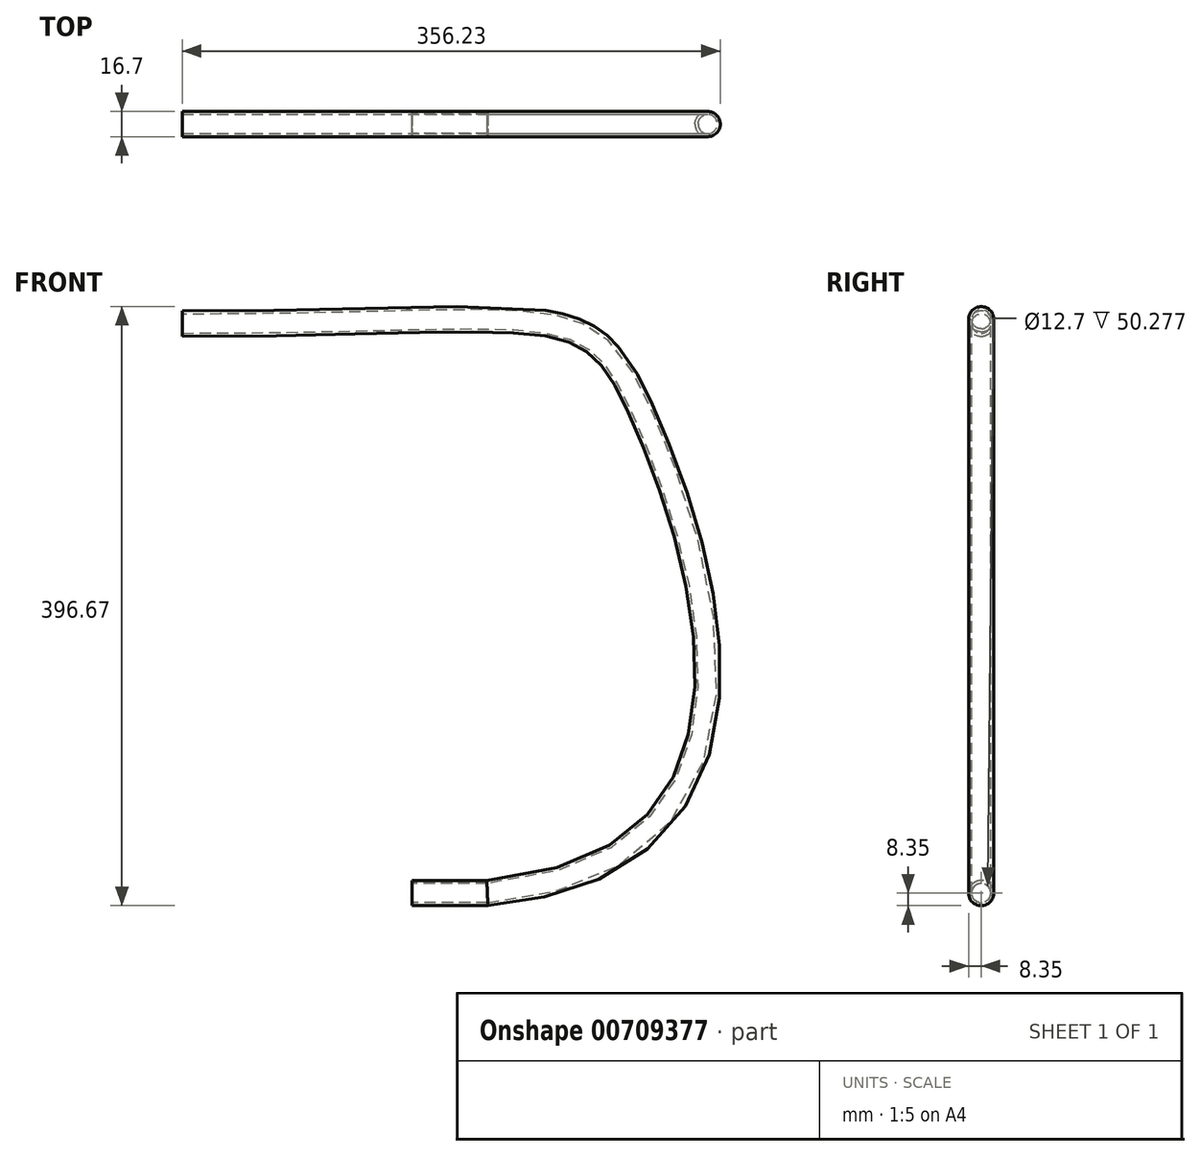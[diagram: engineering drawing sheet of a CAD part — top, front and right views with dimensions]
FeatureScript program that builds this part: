
annotation { "Feature Type Name" : "Feature", "Feature Type Description" : "" }
export const myFeature = defineFeature(function(context is Context, id is Id, definition is map)
    precondition{}
    {
        {
            var Q0;
            Q0=qCreatedBy(makeId("Front.planeOp"),FACE);
            var sketch = newSketch(context, id + "F0", { "sketchPlane" : qUnion([Q0])});
            skPoint(sketch, "E0", {"position": v(-398.72, 63.1) * mm});
            skPoint(sketch, "E1", {"position": v(-246.72, 63.1) * mm});
            skPoint(sketch, "E2", {"position": v(-246.72, -313.9) * mm});
            skLineSegment(sketch, "E3", {"start": v(-246.72, -313.9) * mm, "end": v(-196.72, -313.9) * mm});
            skFitSpline(sketch, "E4", {"points": [v(-398.72, 63.1) * mm, v(-92.27, 0) * mm, v(-196.72, -313.9) * mm], "startDerivative": vector(1557.66, 0) * mm, "endDerivative": vector(-1237.9, -107.97) * mm});
            skSolve(sketch);
        }
        {
            var Q0;
            Q0=sQuery(id+"F0.wireOp",VERTEX,"E0");
            var Q1;
            Q1=qCreatedBy(makeId("Right.planeOp"),FACE);
            cPlane(context, id + "F1", {"entities" : qUnion([Q0, Q1]), "cplaneType" : CPlaneType.PLANE_POINT, "offset" : 25 * mm, "width" : 150 * mm, "height" : 150 * mm});
        }
        {
            var Q0;
            Q0=qCreatedBy(id+"F1.planeOp",FACE);
            var sketch = newSketch(context, id + "F2", { "sketchPlane" : qUnion([Q0])});
            skPoint(sketch, "E5.0", {"position": v(0, 63.1) * mm});
            skCircle(sketch, "E6", {"center": v(0, 63.1) * mm, "radius": 8.35 * mm});
            skCircle(sketch, "E7.0", {"center": v(0, 63.1) * mm, "radius": 6.35 * mm});
            skSolve(sketch);
        }
        {
            var Q0;
            Q0=makeQuery(id+"F2.imprint","IMPRINT",FACE,{"disambiguationData":[TD([[makeQuery(id+"F2.imprint","IMPRINT",EDGE,{"derivedFrom":sQuery(id+"F2.wireOp",EDGE,"E6")}),1.0]])]});
            var Q1;
            Q1=sQuery(id+"F0.wireOp",EDGE,"E4");
            var Q2;
            Q2=sQuery(id+"F0.wireOp",EDGE,"E3");
            sweep(context, id + "F3", {"profiles" : qUnion([Q0]), "path" : qUnion([Q1, Q2])});
        }
    });
